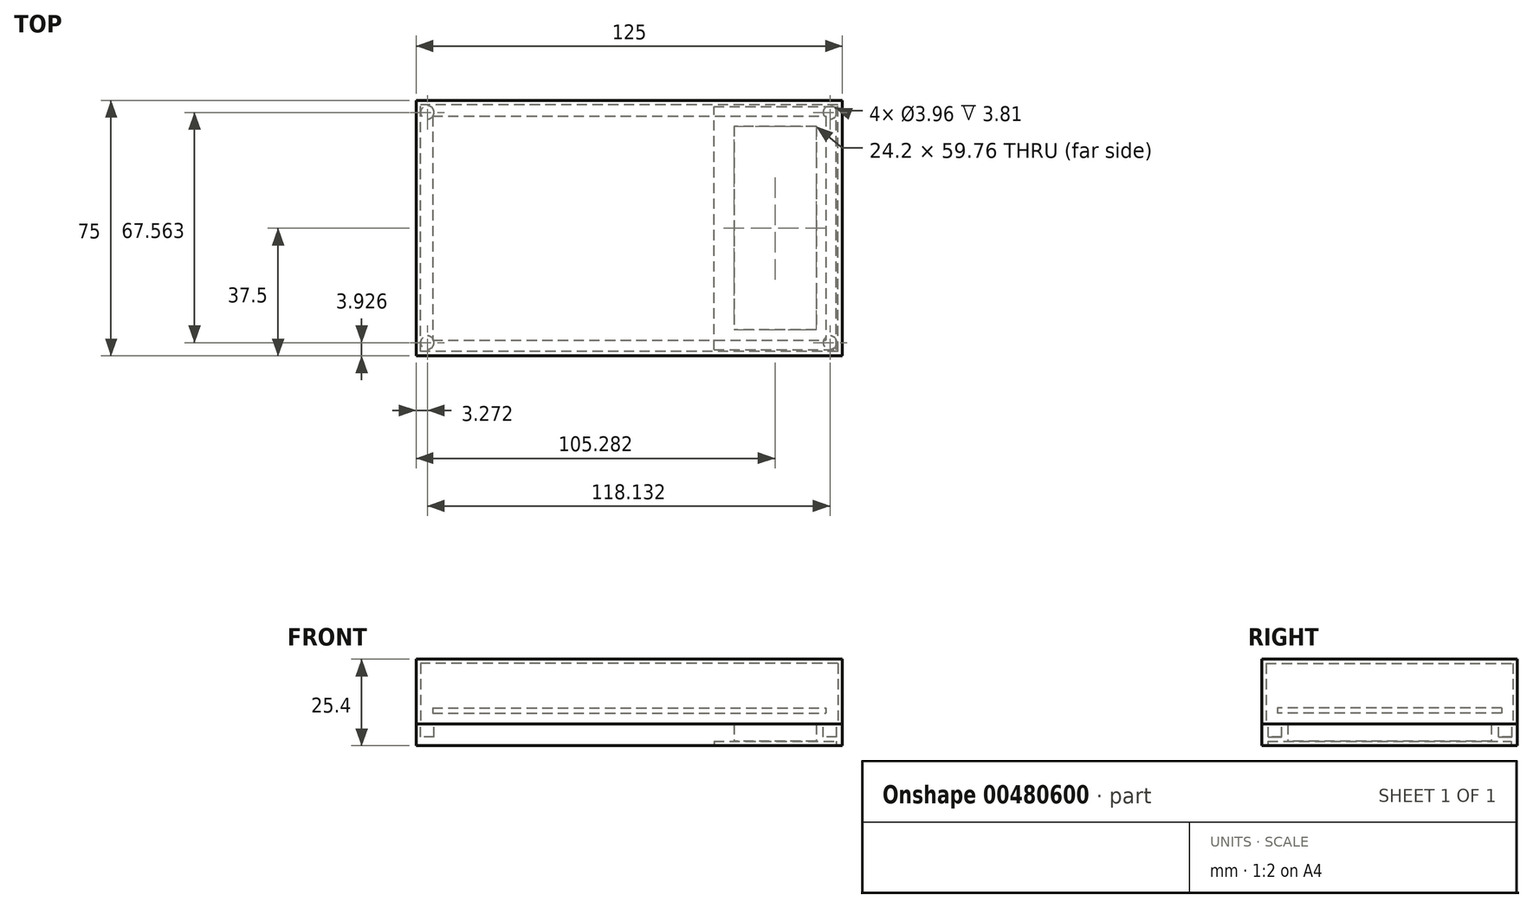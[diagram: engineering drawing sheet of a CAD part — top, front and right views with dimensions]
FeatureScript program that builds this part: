
annotation { "Feature Type Name" : "Feature", "Feature Type Description" : "" }
export const myFeature = defineFeature(function(context is Context, id is Id, definition is map)
    precondition{}
    {
        {
            var Q0;
            Q0=qCreatedBy(makeId("Top.planeOp"),FACE);
            var sketch = newSketch(context, id + "F0", { "sketchPlane" : qUnion([Q0])});
            skLineSegment(sketch, "E0.bottom", {"start": v(62.5, -37.5) * mm, "end": v(-62.5, -37.5) * mm});
            skLineSegment(sketch, "E0.top", {"start": v(62.5, 37.5) * mm, "end": v(-62.5, 37.5) * mm});
            skLineSegment(sketch, "E0.left", {"start": v(62.5, -37.5) * mm, "end": v(62.5, 37.5) * mm});
            skLineSegment(sketch, "E0.right", {"start": v(-62.5, -37.5) * mm, "end": v(-62.5, 37.5) * mm});
            skPoint(sketch, "E0.middle", {"position": v(0, 0) * mm});
            skSolve(sketch);
        }
        {
            var Q0;
            Q0 = qSketchRegion(id + "F0", true);
            extrude(context, id + "F1", {"entities" : qUnion([Q0]), "oppositeDirection" : true, "depth" : 6.35 * mm, "offsetDistance" : 25.4 * mm});
        }
        {
            var Q0;
            Q0=qCreatedBy(makeId("Top.planeOp"),FACE);
            cPlane(context, id + "F2", {"entities" : qUnion([Q0]), "cplaneType" : CPlaneType.OFFSET, "offset" : 3.17 * mm, "width" : 152.4 * mm, "height" : 152.4 * mm});
        }
        {
            var Q0;
            Q0=qCreatedBy(id+"F2.planeOp",FACE);
            var sketch = newSketch(context, id + "F3", { "sketchPlane" : qUnion([Q0])});
            skLineSegment(sketch, "E1.bottom", {"start": v(-57.7, 32.92) * mm, "end": v(57.7, 32.92) * mm});
            skLineSegment(sketch, "E1.top", {"start": v(-57.7, -32.92) * mm, "end": v(57.7, -32.92) * mm});
            skLineSegment(sketch, "E1.left", {"start": v(-57.7, 32.92) * mm, "end": v(-57.7, -32.92) * mm});
            skLineSegment(sketch, "E1.right", {"start": v(57.7, 32.92) * mm, "end": v(57.7, -32.92) * mm});
            skPoint(sketch, "E1.middle", {"position": v(0, 0) * mm});
            skSolve(sketch);
        }
        {
            var Q0;
            Q0 = qSketchRegion(id + "F3", true);
            extrude(context, id + "F4", {"entities" : qUnion([Q0]), "depth" : 1.57 * mm, "offsetDistance" : 25.4 * mm});
        }
        {
            var Q0;
            Q0=qCreatedBy(makeId("Top.planeOp"),FACE);
            var sketch = newSketch(context, id + "F5", { "sketchPlane" : qUnion([Q0])});
            skLineSegment(sketch, "E2.0", {"start": v(-62.5, -37.5) * mm, "end": v(-62.5, 37.5) * mm});
            skLineSegment(sketch, "E2.1", {"start": v(62.5, -37.5) * mm, "end": v(-62.5, -37.5) * mm});
            skLineSegment(sketch, "E2.2", {"start": v(62.5, -37.5) * mm, "end": v(62.5, 37.5) * mm});
            skLineSegment(sketch, "E2.3", {"start": v(62.5, 37.5) * mm, "end": v(-62.5, 37.5) * mm});
            skSolve(sketch);
        }
        {
            var Q0;
            Q0 = qSketchRegion(id + "F5", true);
            extrude(context, id + "F6", {"entities" : qUnion([Q0]), "depth" : 19.05 * mm, "offsetDistance" : 25.4 * mm});
        }
        {
            var Q0;
            Q0=makeQuery(id+"F1.opExtrude","CAP_FACE",FACE,{"disambiguationData":[OSD([sQuery(id+"F0.wireOp",EDGE,"E0.bottom"),sQuery(id+"F0.wireOp",EDGE,"E0.top"),sQuery(id+"F0.wireOp",EDGE,"E0.left"),sQuery(id+"F0.wireOp",EDGE,"E0.right")])],"isStart":false});
            var sketch = newSketch(context, id + "F7", { "sketchPlane" : qUnion([Q0])});
            skLineSegment(sketch, "E3.bottom", {"start": v(30.68, 29.88) * mm, "end": v(54.88, 29.88) * mm});
            skLineSegment(sketch, "E3.top", {"start": v(30.68, -29.88) * mm, "end": v(54.88, -29.88) * mm});
            skLineSegment(sketch, "E3.left", {"start": v(30.68, 29.88) * mm, "end": v(30.68, -29.88) * mm});
            skLineSegment(sketch, "E3.right", {"start": v(54.88, 29.88) * mm, "end": v(54.88, -29.88) * mm});
            skSolve(sketch);
        }
        {
            var Q0;
            Q0 = qSketchRegion(id + "F7", true);
            extrude(context, id + "F8", {"entities" : qUnion([Q0]), "operationType" : NewBodyOperationType.REMOVE, "endBound" : BoundingType.UP_TO_NEXT, "oppositeDirection" : true, "depth" : 25.4 * mm, "offsetDistance" : 25.4 * mm});
        }
        {
            var Q0;
            Q0=makeQuery(id+"F1.opExtrude","CAP_FACE",FACE,{"disambiguationData":[OSD([sQuery(id+"F0.wireOp",EDGE,"E0.bottom"),sQuery(id+"F0.wireOp",EDGE,"E0.top"),sQuery(id+"F0.wireOp",EDGE,"E0.left"),sQuery(id+"F0.wireOp",EDGE,"E0.right")])],"isStart":false});
            var sketch = newSketch(context, id + "F9", { "sketchPlane" : qUnion([Q0])});
            skLineSegment(sketch, "E4.0", {"start": v(24.84, 35.72) * mm, "end": v(24.84, -35.72) * mm});
            skLineSegment(sketch, "E4.1", {"start": v(24.84, 35.72) * mm, "end": v(60.72, 35.72) * mm});
            skLineSegment(sketch, "E4.2", {"start": v(60.72, 35.72) * mm, "end": v(60.72, -35.72) * mm});
            skLineSegment(sketch, "E4.3", {"start": v(24.84, -35.72) * mm, "end": v(60.72, -35.72) * mm});
            skSolve(sketch);
        }
        {
            var Q0;
            Q0 = qSketchRegion(id + "F9", true);
            extrude(context, id + "F10", {"entities" : qUnion([Q0]), "operationType" : NewBodyOperationType.REMOVE, "oppositeDirection" : true, "depth" : 1.27 * mm, "offsetDistance" : 25.4 * mm});
        }
        {
            var Q0;
            Q0 = qSketchRegion(id + "F9", true);
            extrude(context, id + "F11", {"entities" : qUnion([Q0]), "oppositeDirection" : true, "depth" : 1.27 * mm, "offsetDistance" : 25.4 * mm});
        }
        {
            var Q0;
            Q0=makeQuery(id+"F6.opExtrude","CAP_FACE",FACE,{"disambiguationData":[OSD([sQuery(id+"F5.wireOp",EDGE,"E2.0"),sQuery(id+"F5.wireOp",EDGE,"E2.1"),sQuery(id+"F5.wireOp",EDGE,"E2.2"),sQuery(id+"F5.wireOp",EDGE,"E2.3")])],"isStart":true});
            shell(context, id + "F12", {"entities" : qUnion([Q0]), "thickness" : 1.27 * mm});
        }
        {
            var Q0;
            Q0=makeQuery(id+"F1.opExtrude","CAP_FACE",FACE,{"disambiguationData":[OSD([sQuery(id+"F0.wireOp",EDGE,"E0.bottom"),sQuery(id+"F0.wireOp",EDGE,"E0.top"),sQuery(id+"F0.wireOp",EDGE,"E0.left"),sQuery(id+"F0.wireOp",EDGE,"E0.right")])],"isStart":true});
            var sketch = newSketch(context, id + "F13", { "sketchPlane" : qUnion([Q0])});
            skCircle(sketch, "E5", {"center": v(58.9, 33.99) * mm, "radius": 1.98 * mm});
            skCircle(sketch, "E6", {"center": v(58.9, -33.57) * mm, "radius": 1.98 * mm});
            skCircle(sketch, "E7", {"center": v(-59.23, -33.57) * mm, "radius": 1.98 * mm});
            skCircle(sketch, "E8", {"center": v(-59.23, 33.99) * mm, "radius": 1.98 * mm});
            skLineSegment(sketch, "E9", {"start": v(-59.23, 33.99) * mm, "end": v(58.9, 33.99) * mm, "construction": true});
            skLineSegment(sketch, "E10", {"start": v(58.9, -33.57) * mm, "end": v(58.9, 33.99) * mm, "construction": true});
            skLineSegment(sketch, "E11", {"start": v(58.9, -33.57) * mm, "end": v(-59.23, -33.57) * mm, "construction": true});
            skLineSegment(sketch, "E12", {"start": v(-59.23, 33.99) * mm, "end": v(-59.23, -33.57) * mm, "construction": true});
            skSolve(sketch);
        }
        {
            var Q0;
            Q0 = qSketchRegion(id + "F13", true);
            extrude(context, id + "F14", {"entities" : qUnion([Q0]), "operationType" : NewBodyOperationType.REMOVE, "oppositeDirection" : true, "depth" : 3.8 * mm, "offsetDistance" : 25.4 * mm});
        }
    });
